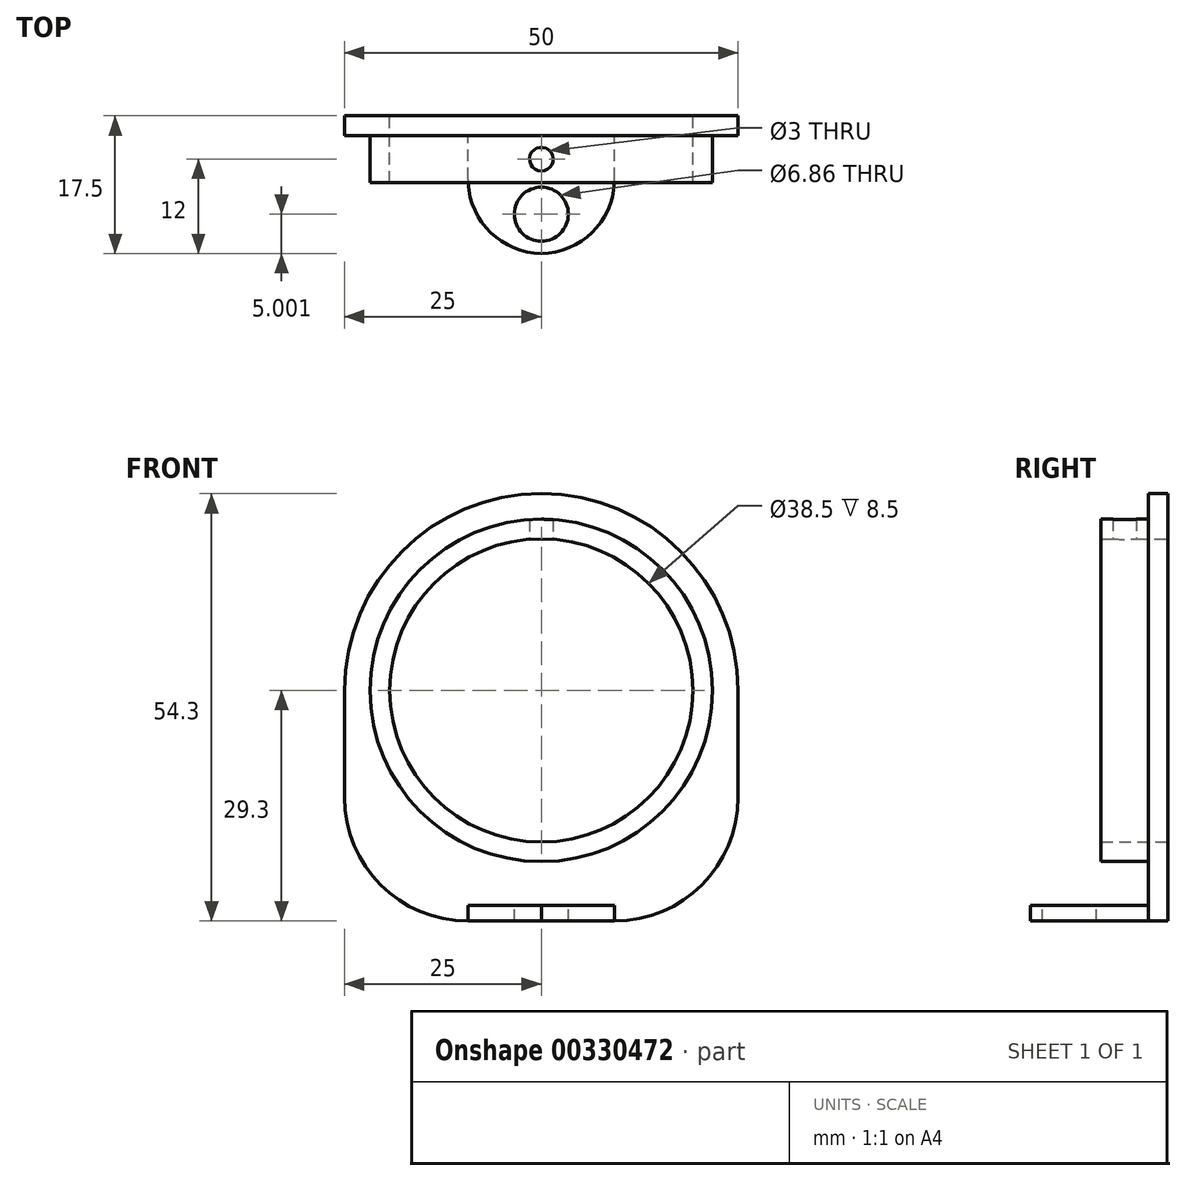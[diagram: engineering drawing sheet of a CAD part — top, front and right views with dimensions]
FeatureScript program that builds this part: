
annotation { "Feature Type Name" : "Feature", "Feature Type Description" : "" }
export const myFeature = defineFeature(function(context is Context, id is Id, definition is map)
    precondition{}
    {
        {
            var Q0;
            Q0=qCreatedBy(makeId("Front.planeOp"),FACE);
            var sketch = newSketch(context, id + "F0", { "sketchPlane" : qUnion([Q0])});
            skCircle(sketch, "E0", {"center": v(0, 0) * mm, "radius": 21.75 * mm});
            skCircle(sketch, "E1.0", {"center": v(0, 0) * mm, "radius": 19.25 * mm});
            skSolve(sketch);
        }
        {
            var Q0;
            Q0=qSketchRegion(id+"F0",true);
            extrude(context, id + "F1", {"entities" : qUnion([Q0]), "depth" : 6 * mm});
        }
        {
            var Q0;
            Q0=qCreatedBy(makeId("Front.planeOp"),FACE);
            var sketch = newSketch(context, id + "F2", { "sketchPlane" : qUnion([Q0])});
            skCircle(sketch, "E2", {"center": v(0, 0) * mm, "radius": 25 * mm});
            skLineSegment(sketch, "E3", {"start": v(-25, 0) * mm, "end": v(-25, -29.3) * mm});
            skLineSegment(sketch, "E4", {"start": v(-25, -29.3) * mm, "end": v(25, -29.3) * mm});
            skLineSegment(sketch, "E5", {"start": v(25, -29.3) * mm, "end": v(25, 0) * mm});
            skSolve(sketch);
        }
        {
            var Q0;
            Q0=qSketchRegion(id+"F2",true);
            extrude(context, id + "F3", {"entities" : qUnion([Q0]), "operationType" : NewBodyOperationType.ADD, "oppositeDirection" : true, "depth" : 2.5 * mm});
        }
        {
            var Q0;
            Q0=qCreatedBy(makeId("Front.planeOp"),FACE);
            var sketch = newSketch(context, id + "F4", { "sketchPlane" : qUnion([Q0])});
            skCircle(sketch, "E6", {"center": v(0, 0) * mm, "radius": 19.25 * mm});
            skSolve(sketch);
        }
        {
            var Q0;
            Q0=qSketchRegion(id+"F4",true);
            extrude(context, id + "F5", {"entities" : qUnion([Q0]), "operationType" : NewBodyOperationType.REMOVE, "oppositeDirection" : true, "depth" : 25 * mm});
        }
        {
            var Q0;
            Q0=qCreatedBy(makeId("Top.planeOp"),FACE);
            var sketch = newSketch(context, id + "F6", { "sketchPlane" : qUnion([Q0])});
            skCircle(sketch, "E7", {"center": v(0, -3) * mm, "radius": 1.5 * mm});
            skSolve(sketch);
        }
        {
            var Q0;
            Q0=qSketchRegion(id+"F6",true);
            extrude(context, id + "F7", {"entities" : qUnion([Q0]), "operationType" : NewBodyOperationType.REMOVE, "depth" : 25 * mm});
        }
        {
            var Q0;
            {var subQ0=sQuery(id+"F2.wireOp",EDGE,"E4");var subQ1=sQuery(id+"F2.wireOp",EDGE,"E3");var subQ2=sQuery(id+"F2.wireOp",EDGE,"E2");var subQ3=sQuery(id+"F2.wireOp",EDGE,"E5");Q0=makeQuery(id+"F3.boolean.opBoolean","SPLIT",FACE,{"disambiguationData":[TD([makeQuery(id+"F1.opExtrude","SWEPT_FACE",FACE,{"disambiguationData":[OSD([sQuery(id+"F0.wireOp",EDGE,"E0")])]})])],"derivedFrom":makeQuery(id+"F3.opExtrude","CAP_FACE",FACE,{"disambiguationData":[OSD([subQ2,subQ1,subQ0,subQ3])],"isStart":true})});}
            var sketch = newSketch(context, id + "F8", { "sketchPlane" : qUnion([Q0])});
            skLineSegment(sketch, "E8.bottom", {"start": v(9.3, -29.3) * mm, "end": v(-9.3, -29.3) * mm});
            skLineSegment(sketch, "E8.top", {"start": v(9.3, -27.3) * mm, "end": v(-9.3, -27.3) * mm});
            skLineSegment(sketch, "E8.left", {"start": v(9.3, -29.3) * mm, "end": v(9.3, -27.3) * mm});
            skLineSegment(sketch, "E8.right", {"start": v(-9.3, -29.3) * mm, "end": v(-9.3, -27.3) * mm});
            skPoint(sketch, "E8.middle", {"position": v(0, -28.3) * mm});
            skPoint(sketch, "E8.middle.positionSnap0", {"position": v(0, -29.3) * mm});
            skPoint(sketch, "E8.centerSnap0", {"position": v(0, -29.3) * mm});
            skSolve(sketch);
        }
        {
            var Q0;
            Q0 = qSketchRegion(id + "F8", true);
            extrude(context, id + "F9", {"entities" : qUnion([Q0]), "operationType" : NewBodyOperationType.ADD, "depth" : 15 * mm});
        }
        {
            var Q0;
            Q0=makeQuery(id+"F3.opExtrude","SWEPT_EDGE",EDGE,{"disambiguationData":[OSD([sQuery(id+"F2.wireOp",EDGE,"E3"),sQuery(id+"F2.wireOp",EDGE,"E4")])]});
            var Q1;
            Q1=makeQuery(id+"F3.opExtrude","SWEPT_EDGE",EDGE,{"disambiguationData":[OSD([sQuery(id+"F2.wireOp",EDGE,"E4"),sQuery(id+"F2.wireOp",EDGE,"E5")])]});
            fillet(context, id + "F10", {"entities" : qUnion([Q0, Q1]), "radius" : 15.7 * mm, "tangentPropagation" : true, "allowEdgeOverflow" : false});
        }
        {
            var Q0;
            Q0=makeQuery(id+"F9.opExtrude","CAP_EDGE",EDGE,{"disambiguationData":[OSD([sQuery(id+"F8.wireOp",EDGE,"E8.left")])],"isStart":false});
            var Q1;
            Q1=makeQuery(id+"F9.opExtrude","CAP_EDGE",EDGE,{"disambiguationData":[OSD([sQuery(id+"F8.wireOp",EDGE,"E8.right")])],"isStart":false});
            fillet(context, id + "F11", {"entities" : qUnion([Q0, Q1]), "radius" : 9.42 * mm, "tangentPropagation" : true, "allowEdgeOverflow" : false});
        }
        {
            var Q0;
            Q0=makeQuery(id+"F9.opExtrude","SWEPT_FACE",FACE,{"disambiguationData":[OSD([sQuery(id+"F8.wireOp",EDGE,"E8.top")])]});
            var sketch = newSketch(context, id + "F12", { "sketchPlane" : qUnion([Q0])});
            skCircle(sketch, "E9", {"center": v(0, -10) * mm, "radius": 3.43 * mm});
            skSolve(sketch);
        }
        {
            var Q0;
            Q0 = qSketchRegion(id + "F12", true);
            extrude(context, id + "F13", {"entities" : qUnion([Q0]), "operationType" : NewBodyOperationType.REMOVE, "oppositeDirection" : true, "depth" : 25 * mm});
        }
    });
